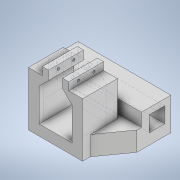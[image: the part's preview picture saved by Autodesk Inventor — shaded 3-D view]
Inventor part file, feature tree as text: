
AUTODESK INVENTOR PART (.ipt)
format: ipt  version: 2021 (Build 250183000, 183)  size: 202,240 bytes
history: native  units: mm
features: extrude x6, sketch x6, chamfer x3
ambient origin geometry x8: Origin, YZ Plane, XZ Plane, XY Plane, X Axis, Y Axis, Z Axis, Center Point
bodies: Solid1 (feature_tree)
feature tree (15):
  extrude  "Extrusion1"  Depth=42.5mm
  extrude  "Extrusion5"  Depth=45.0mm TaperAngle=0.0deg
  extrude  "Extrusion6"  Depth=20.1mm
  extrude  "Extrusion7"  Depth=42.0mm
  extrude  "Extrusion8"  Depth=120.0mm TaperAngle=0.0deg
  extrude  "Extrusion9"  Depth=18.0mm TaperAngle=0.0deg
  chamfer  "Chamfer1"  Distance=8.0mm
  chamfer  "Chamfer2"  Distance=6.0mm
  chamfer  "Chamfer3"  Distance=25.0mm
  sketch  "Sketch1"  dims[d0=42.5mm d1=9.0mm]
  sketch  "Sketch4"  dims[d3=70.0mm d4=45.0mm d5=0.0mm]
  sketch  "Sketch5"  dims[d17=18.0mm d18=20.1mm]
  sketch  "Sketch6"  dims[d20=14.0mm d21=42.0mm]
  sketch  "Sketch7"  dims[d22=38.0mm d23=120.0mm d24=0.0mm]
  sketch  "Sketch8"  dims[d25=15.0mm d27=4.3mm d28=18.0mm d29=0.0mm d30=8.0mm d31=6.0mm d32=25.0mm d33=25.0mm d34=25.0mm d35=45.0deg d36=35.0mm d37=25.0mm d38=45.0deg d39=8.0mm d40=10.0mm d41=0.0mm d42=20.0mm d43=10.0mm d44=5.0mm d45=3.2mm d46=0.0mm d47=0.0mm d48=4.2mm d49=6.0mm d50=0.0mm d58=15.0mm d59=15.0mm d60=12.25mm d61=25.0mm d62=45.0deg]
